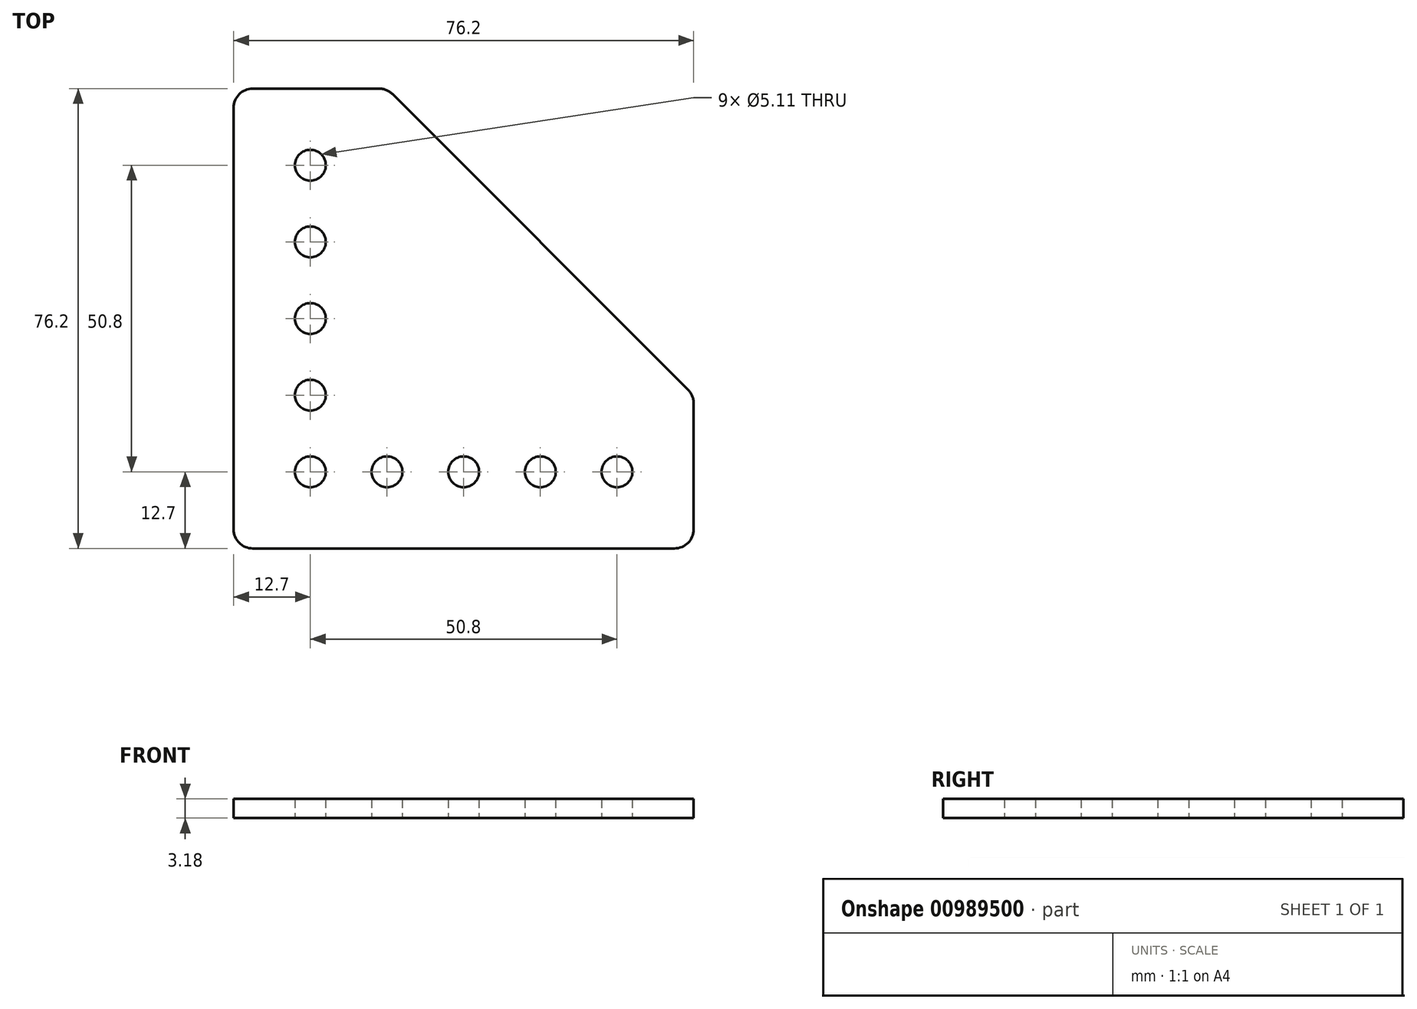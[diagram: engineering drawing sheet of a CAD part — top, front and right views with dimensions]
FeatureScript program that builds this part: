
annotation { "Feature Type Name" : "Feature", "Feature Type Description" : "" }
export const myFeature = defineFeature(function(context is Context, id is Id, definition is map)
    precondition{}
    {
        {
            var Q0;
            Q0=qCreatedBy(makeId("Top.planeOp"),FACE);
            var sketch = newSketch(context, id + "F0", { "sketchPlane" : qUnion([Q0])});
            skCircle(sketch, "E0", {"center": v(0, 0) * mm, "radius": 2.55 * mm});
            skCircle(sketch, "E1", {"center": v(0, 12.7) * mm, "radius": 2.55 * mm});
            skCircle(sketch, "E2", {"center": v(0, 25.4) * mm, "radius": 2.55 * mm});
            skCircle(sketch, "E3", {"center": v(0, 38.1) * mm, "radius": 2.55 * mm});
            skCircle(sketch, "E4", {"center": v(0, 50.8) * mm, "radius": 2.55 * mm});
            skCircle(sketch, "E5", {"center": v(12.7, 0) * mm, "radius": 2.55 * mm});
            skCircle(sketch, "E6", {"center": v(25.4, 0) * mm, "radius": 2.55 * mm});
            skCircle(sketch, "E7", {"center": v(38.1, 0) * mm, "radius": 2.55 * mm});
            skCircle(sketch, "E8", {"center": v(50.8, 0) * mm, "radius": 2.55 * mm});
            skLineSegment(sketch, "E9", {"start": v(12.7, 0) * mm, "end": v(0, 0) * mm, "construction": true});
            skLineSegment(sketch, "E10", {"start": v(0, 0) * mm, "end": v(0, 12.7) * mm, "construction": true});
            skLineSegment(sketch, "E11", {"start": v(-12.7, 63.5) * mm, "end": v(-12.7, -12.7) * mm});
            skLineSegment(sketch, "E12", {"start": v(-12.7, -12.7) * mm, "end": v(63.5, -12.7) * mm});
            skLineSegment(sketch, "E13", {"start": v(63.5, -12.7) * mm, "end": v(63.5, 12.7) * mm});
            skLineSegment(sketch, "E14", {"start": v(63.5, 12.7) * mm, "end": v(12.7, 63.5) * mm});
            skLineSegment(sketch, "E15", {"start": v(12.7, 63.5) * mm, "end": v(-12.7, 63.5) * mm});
            skSolve(sketch);
        }
        {
            var Q0;
            Q0 = qSketchRegion(id + "F0", true);
            extrude(context, id + "F1", {"entities" : qUnion([Q0]), "depth" : 3.17 * mm, "offsetDistance" : 25.4 * mm});
        }
        {
            var Q0;
            Q0=makeQuery(id+"F1.opExtrude","SWEPT_EDGE",EDGE,{"disambiguationData":[OSD([sQuery(id+"F0.wireOp",EDGE,"E11"),sQuery(id+"F0.wireOp",EDGE,"E15")])]});
            var Q1;
            Q1=makeQuery(id+"F1.opExtrude","SWEPT_EDGE",EDGE,{"disambiguationData":[OSD([sQuery(id+"F0.wireOp",EDGE,"E14"),sQuery(id+"F0.wireOp",EDGE,"E15")])]});
            var Q2;
            Q2=makeQuery(id+"F1.opExtrude","SWEPT_EDGE",EDGE,{"disambiguationData":[OSD([sQuery(id+"F0.wireOp",EDGE,"E11"),sQuery(id+"F0.wireOp",EDGE,"E12")])]});
            var Q3;
            Q3=makeQuery(id+"F1.opExtrude","SWEPT_EDGE",EDGE,{"disambiguationData":[OSD([sQuery(id+"F0.wireOp",EDGE,"E12"),sQuery(id+"F0.wireOp",EDGE,"E13")])]});
            var Q4;
            Q4=makeQuery(id+"F1.opExtrude","SWEPT_EDGE",EDGE,{"disambiguationData":[OSD([sQuery(id+"F0.wireOp",EDGE,"E13"),sQuery(id+"F0.wireOp",EDGE,"E14")])]});
            fillet(context, id + "F2", {"entities" : qUnion([Q0, Q1, Q2, Q3, Q4]), "radius" : 3.17 * mm, "tangentPropagation" : true, "allowEdgeOverflow" : false});
        }
    });
